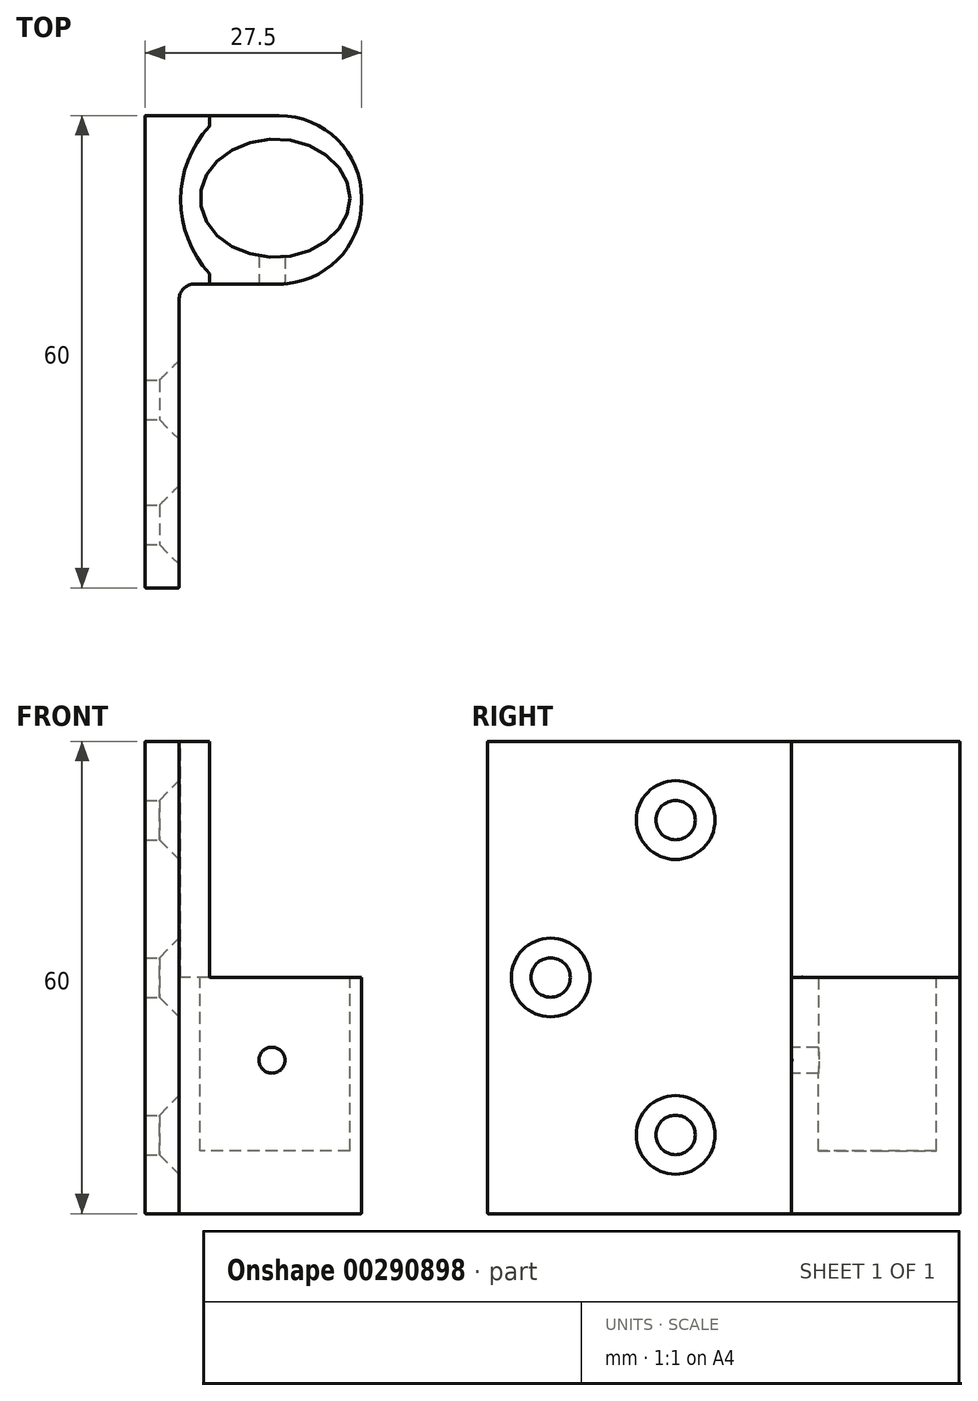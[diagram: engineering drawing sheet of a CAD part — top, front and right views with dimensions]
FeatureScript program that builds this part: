
annotation { "Feature Type Name" : "Feature", "Feature Type Description" : "" }
export const myFeature = defineFeature(function(context is Context, id is Id, definition is map)
    precondition{}
    {
        {
            var Q0;
            Q0=qCreatedBy(makeId("Top.planeOp"),FACE);
            var sketch = newSketch(context, id + "F0", { "sketchPlane" : qUnion([Q0])});
            skLineSegment(sketch, "E0", {"start": v(23.73, 6) * mm, "end": v(23.73, 6.4) * mm});
            skArc(sketch, "E1.filletArc", {"start": v(13.23, -4.5) * mm, "mid": v(20.66, -1.43) * mm, "end": v(23.73, 6) * mm});
            skArc(sketch, "E2.filletArc", {"start": v(23.73, 6.4) * mm, "mid": v(20.66, 13.82) * mm, "end": v(13.23, 16.9) * mm});
            skLineSegment(sketch, "E3.bottom", {"start": v(-3.77, -43.1) * mm, "end": v(0.53, -43.1) * mm});
            skLineSegment(sketch, "E3.left", {"start": v(-3.77, -43.1) * mm, "end": v(-3.77, 16.9) * mm});
            skLineSegment(sketch, "E3.right", {"start": v(0.53, -43.1) * mm, "end": v(0.53, -6.5) * mm});
            skLineSegment(sketch, "E4", {"start": v(-3.77, 16.9) * mm, "end": v(13.23, 16.9) * mm});
            skLineSegment(sketch, "E5", {"start": v(13.23, -4.5) * mm, "end": v(2.53, -4.5) * mm});
            skPoint(sketch, "E6.visualSharp", {"position": v(0.53, -4.5) * mm});
            skArc(sketch, "E6.filletArc", {"start": v(2.53, -4.5) * mm, "mid": v(1.12, -5.1) * mm, "end": v(0.53, -6.5) * mm});
            skSolve(sketch);
        }
        {
            var Q0;
            Q0 = qSketchRegion(id + "F0", true);
            extrude(context, id + "F1", {"entities" : qUnion([Q0]), "depth" : 60 * mm});
        }
        {
            var Q0;
            Q0=makeQuery(id+"F1.opExtrude","CAP_FACE",FACE,{"disambiguationData":[OSD([sQuery(id+"F0.wireOp",EDGE,"E0"),sQuery(id+"F0.wireOp",EDGE,"E1.filletArc"),sQuery(id+"F0.wireOp",EDGE,"E2.filletArc"),sQuery(id+"F0.wireOp",EDGE,"E3.bottom"),sQuery(id+"F0.wireOp",EDGE,"E3.left"),sQuery(id+"F0.wireOp",EDGE,"E3.right"),sQuery(id+"F0.wireOp",EDGE,"E4"),sQuery(id+"F0.wireOp",EDGE,"E5"),sQuery(id+"F0.wireOp",EDGE,"E6.filletArc")])],"isStart":false});
            var sketch = newSketch(context, id + "F2", { "sketchPlane" : qUnion([Q0])});
            skLineSegment(sketch, "E7", {"start": v(4.43, 16.9) * mm, "end": v(4.43, 15.6) * mm});
            skLineSegment(sketch, "E8", {"start": v(-3.77, -4.5) * mm, "end": v(4.43, -4.5) * mm});
            skArc(sketch, "E9", {"start": v(4.43, 15.6) * mm, "mid": v(0.73, 6.2) * mm, "end": v(4.43, -3.2) * mm});
            skLineSegment(sketch, "E10", {"start": v(4.43, 16.9) * mm, "end": v(-3.77, 16.9) * mm});
            skLineSegment(sketch, "E11", {"start": v(-3.77, 16.9) * mm, "end": v(-3.77, -4.5) * mm});
            skLineSegment(sketch, "E12.trimOffspring", {"start": v(4.43, -3.2) * mm, "end": v(4.43, -4.5) * mm});
            skSolve(sketch);
        }
        {
            var Q0;
            {var subQ3=sQuery(id+"F2.wireOp",EDGE,"E7");Q0=makeQuery(id+"F2.imprint","IMPRINT",FACE,{"disambiguationData":[TD([[makeQuery(id+"F2.imprint","IMPRINT",EDGE,{"derivedFrom":subQ3}),1.0]])]});}
            extrude(context, id + "F3", {"entities" : qUnion([Q0]), "operationType" : NewBodyOperationType.REMOVE, "oppositeDirection" : true, "depth" : 30 * mm});
        }
        {
            var Q0;
            Q0=makeQuery(id+"F3.boolean.opBoolean","COPY",FACE,{"derivedFrom":makeQuery(id+"F3.opExtrude","CAP_FACE",FACE,{"disambiguationData":[OSD([sQuery(id+"F0.wireOp",EDGE,"E0"),sQuery(id+"F0.wireOp",EDGE,"E1.filletArc"),sQuery(id+"F0.wireOp",EDGE,"E2.filletArc"),sQuery(id+"F0.wireOp",EDGE,"E4"),sQuery(id+"F0.wireOp",EDGE,"E5"),sQuery(id+"F2.wireOp",EDGE,"E7"),sQuery(id+"F2.wireOp",EDGE,"E9"),sQuery(id+"F2.wireOp",EDGE,"E12.trimOffspring")])],"isStart":false})});
            var sketch = newSketch(context, id + "F4", { "sketchPlane" : qUnion([Q0])});
            skEllipse(sketch, "E13", {"center": v(12.73, 6.4) * mm, "majorRadius": 9.5 * mm, "minorRadius": 7.5 * mm, "majorAxis": v(1, 0)});
            skSolve(sketch);
        }
        {
            var Q0;
            Q0=makeQuery(id+"F4.imprint","IMPRINT",FACE,{"disambiguationData":[TD([[makeQuery(id+"F4.imprint","IMPRINT",EDGE,{"derivedFrom":sQuery(id+"F4.wireOp",EDGE,"E13")}),1.0]])]});
            extrude(context, id + "F5", {"entities" : qUnion([Q0]), "operationType" : NewBodyOperationType.REMOVE, "oppositeDirection" : true, "depth" : 22 * mm});
        }
        {
            var Q0;
            Q0=makeQuery(id+"F1.opExtrude","SWEPT_FACE",FACE,{"disambiguationData":[OSD([sQuery(id+"F0.wireOp",EDGE,"E5")])]});
            var sketch = newSketch(context, id + "F6", { "sketchPlane" : qUnion([Q0])});
            skCircle(sketch, "E14", {"center": v(12.33, 19.5) * mm, "radius": 1.5 * mm});
            skSolve(sketch);
        }
        {
            var Q0;
            Q0=sQuery(id+"F6.wireOp",VERTEX,"E14.center");
            var Q1;
            Q1=makeQuery(id+"F1.opExtrude","SWEPT_BODY",BODY,{"disambiguationData":[OSD([sQuery(id+"F0.wireOp",EDGE,"E0"),sQuery(id+"F0.wireOp",EDGE,"E1.filletArc"),sQuery(id+"F0.wireOp",EDGE,"E2.filletArc"),sQuery(id+"F0.wireOp",EDGE,"E3.bottom"),sQuery(id+"F0.wireOp",EDGE,"E3.left"),sQuery(id+"F0.wireOp",EDGE,"E3.right"),sQuery(id+"F0.wireOp",EDGE,"E4"),sQuery(id+"F0.wireOp",EDGE,"E5"),sQuery(id+"F0.wireOp",EDGE,"E6.filletArc")])]});
            hole(context, id + "F7", {"style" : HoleStyle.SIMPLE, "endStyle" : HoleEndStyle.BLIND, "standardTappedOrClearance" : lookupTablePath({ "standard" : "ISO", "fit" : "Normal", "size" : "M3", "type" : "Clearance" }), "standardBlindInLast" : lookupTablePath({ "fit" : "Standard", "standard" : "ISO", "size" : "M3", "type" : "Clearance" }), "holeDiameter" : 3.3 * mm, "holeDepth" : 8 * mm, "tappedDepth" : 10 * mm, "tapClearance" : 3, "locations" : qUnion([Q0]), "scope" : qUnion([Q1])});
        }
        {
            var Q0;
            Q0=makeQuery(id+"F1.opExtrude","SWEPT_FACE",FACE,{"disambiguationData":[OSD([sQuery(id+"F0.wireOp",EDGE,"E3.right")])]});
            var sketch = newSketch(context, id + "F8", { "sketchPlane" : qUnion([Q0])});
            skCircle(sketch, "E15", {"center": v(-19.23, 50) * mm, "radius": 2.5 * mm});
            skCircle(sketch, "E16", {"center": v(-35.1, 30) * mm, "radius": 2.5 * mm});
            skCircle(sketch, "E17", {"center": v(-19.23, 10) * mm, "radius": 2.5 * mm});
            skSolve(sketch);
        }
        {
            var Q0;
            Q0=sQuery(id+"F8.wireOp",VERTEX,"E15.center");
            var Q1;
            Q1=sQuery(id+"F8.wireOp",VERTEX,"E16.center");
            var Q2;
            Q2=sQuery(id+"F8.wireOp",VERTEX,"E17.center");
            var Q3;
            Q3=makeQuery(id+"F1.opExtrude","SWEPT_BODY",BODY,{"disambiguationData":[OSD([sQuery(id+"F0.wireOp",EDGE,"E0"),sQuery(id+"F0.wireOp",EDGE,"E1.filletArc"),sQuery(id+"F0.wireOp",EDGE,"E2.filletArc"),sQuery(id+"F0.wireOp",EDGE,"E3.bottom"),sQuery(id+"F0.wireOp",EDGE,"E3.left"),sQuery(id+"F0.wireOp",EDGE,"E3.right"),sQuery(id+"F0.wireOp",EDGE,"E4"),sQuery(id+"F0.wireOp",EDGE,"E5"),sQuery(id+"F0.wireOp",EDGE,"E6.filletArc")])]});
            hole(context, id + "F9", {"style" : HoleStyle.C_SINK, "endStyle" : HoleEndStyle.THROUGH, "holeDiameter" : 5 * mm, "cSinkDiameter" : 10 * mm, "cSinkAngle" : 90 * degree, "tappedDepth" : 10 * mm, "tapClearance" : 3, "locations" : qUnion([Q0, Q1, Q2]), "scope" : qUnion([Q3])});
        }
        {
            var Q0;
            Q0=makeQuery(id+"F1.opExtrude","CAP_EDGE",EDGE,{"disambiguationData":[OSD([sQuery(id+"F0.wireOp",EDGE,"E3.right")])],"isStart":false});
            var Q1;
            Q1=makeQuery(id+"F1.opExtrude","SWEPT_EDGE",EDGE,{"disambiguationData":[OSD([sQuery(id+"F0.wireOp",EDGE,"E3.bottom"),sQuery(id+"F0.wireOp",EDGE,"E3.right")])]});
            var Q2;
            Q2=makeQuery(id+"F1.opExtrude","CAP_EDGE",EDGE,{"disambiguationData":[OSD([sQuery(id+"F0.wireOp",EDGE,"E3.bottom")])],"isStart":false});
            var Q3;
            Q3=makeQuery(id+"F1.opExtrude","SWEPT_EDGE",EDGE,{"disambiguationData":[OSD([sQuery(id+"F0.wireOp",EDGE,"E3.bottom"),sQuery(id+"F0.wireOp",EDGE,"E3.left")])]});
            var Q4;
            Q4=makeQuery(id+"F1.opExtrude","CAP_EDGE",EDGE,{"disambiguationData":[OSD([sQuery(id+"F0.wireOp",EDGE,"E3.left")])],"isStart":false});
            var Q5;
            Q5=makeQuery(id+"F1.opExtrude","CAP_EDGE",EDGE,{"disambiguationData":[OSD([sQuery(id+"F0.wireOp",EDGE,"E3.bottom")])],"isStart":true});
            var Q6;
            Q6=makeQuery(id+"F1.opExtrude","CAP_EDGE",EDGE,{"disambiguationData":[OSD([sQuery(id+"F0.wireOp",EDGE,"E3.right")])],"isStart":true});
            var Q7;
            Q7=makeQuery(id+"F1.opExtrude","CAP_EDGE",EDGE,{"disambiguationData":[OSD([sQuery(id+"F0.wireOp",EDGE,"E3.left")])],"isStart":true});
            var Q8;
            Q8=makeQuery(id+"F1.opExtrude","SWEPT_EDGE",EDGE,{"disambiguationData":[OSD([sQuery(id+"F0.wireOp",EDGE,"E3.left"),sQuery(id+"F0.wireOp",EDGE,"E4")])]});
            var Q9;
            Q9=makeQuery(id+"F1.opExtrude","CAP_EDGE",EDGE,{"disambiguationData":[OSD([sQuery(id+"F0.wireOp",EDGE,"E4")])],"isStart":false});
            var Q10;
            Q10=makeQuery(id+"F3.boolean.opBoolean","COPY",EDGE,{"derivedFrom":makeQuery(id+"F3.opExtrude","CAP_EDGE",EDGE,{"disambiguationData":[OSD([sQuery(id+"F2.wireOp",EDGE,"E7")])],"isStart":true})});
            var Q11;
            Q11=makeQuery(id+"F1.opExtrude","CAP_EDGE",EDGE,{"disambiguationData":[OSD([sQuery(id+"F0.wireOp",EDGE,"E4")])],"isStart":true});
            var Q12;
            Q12=makeQuery(id+"F3.boolean.opBoolean","COPY",EDGE,{"derivedFrom":makeQuery(id+"F3.opExtrude","CAP_EDGE",EDGE,{"disambiguationData":[OSD([sQuery(id+"F0.wireOp",EDGE,"E4")])],"isStart":false})});
            var Q13;
            Q13=makeQuery(id+"F5.boolean.opBoolean","COPY",EDGE,{"derivedFrom":makeQuery(id+"F5.opExtrude","CAP_EDGE",EDGE,{"disambiguationData":[OSD([sQuery(id+"F4.wireOp",EDGE,"E13")])],"isStart":true})});
            var Q14;
            Q14=makeQuery(id+"F3.boolean.opBoolean","COPY",EDGE,{"derivedFrom":makeQuery(id+"F3.opExtrude","SWEPT_EDGE",EDGE,{"disambiguationData":[OSD([sQuery(id+"F0.wireOp",EDGE,"E4"),sQuery(id+"F2.wireOp",EDGE,"E7"),sQuery(id+"F2.wireOp",EDGE,"E10")])]})});
            var Q15;
            Q15=makeQuery(id+"F3.boolean.opBoolean","COPY",EDGE,{"derivedFrom":makeQuery(id+"F3.opExtrude","SWEPT_EDGE",EDGE,{"disambiguationData":[OSD([sQuery(id+"F0.wireOp",EDGE,"E5"),sQuery(id+"F2.wireOp",EDGE,"E8"),sQuery(id+"F2.wireOp",EDGE,"E12.trimOffspring")])]})});
            var Q16;
            Q16=makeQuery(id+"F3.boolean.opBoolean","COPY",EDGE,{"derivedFrom":makeQuery(id+"F3.opExtrude","CAP_EDGE",EDGE,{"disambiguationData":[OSD([sQuery(id+"F2.wireOp",EDGE,"E12.trimOffspring")])],"isStart":false})});
            var Q17;
            Q17=makeQuery(id+"F3.boolean.opBoolean","COPY",EDGE,{"derivedFrom":makeQuery(id+"F3.opExtrude","CAP_EDGE",EDGE,{"disambiguationData":[OSD([sQuery(id+"F2.wireOp",EDGE,"E7")])],"isStart":false})});
            var Q18;
            Q18=makeQuery(id+"F3.boolean.opBoolean","COPY",EDGE,{"derivedFrom":makeQuery(id+"F3.opExtrude","CAP_EDGE",EDGE,{"disambiguationData":[OSD([sQuery(id+"F2.wireOp",EDGE,"E12.trimOffspring")])],"isStart":true})});
            var Q19;
            Q19=makeQuery(id+"F3.boolean.opBoolean","COPY",EDGE,{"derivedFrom":makeQuery(id+"F3.opExtrude","CAP_EDGE",EDGE,{"disambiguationData":[OSD([sQuery(id+"F2.wireOp",EDGE,"E9")])],"isStart":true})});
            var Q20;
            Q20=makeQuery(id+"F3.boolean.opBoolean","COPY",EDGE,{"derivedFrom":makeQuery(id+"F3.opExtrude","SWEPT_EDGE",EDGE,{"disambiguationData":[OSD([sQuery(id+"F2.wireOp",EDGE,"E7"),sQuery(id+"F2.wireOp",EDGE,"E9")])]})});
            var Q21;
            Q21=makeQuery(id+"F3.boolean.opBoolean","COPY",EDGE,{"derivedFrom":makeQuery(id+"F3.opExtrude","SWEPT_EDGE",EDGE,{"disambiguationData":[OSD([sQuery(id+"F2.wireOp",EDGE,"E9"),sQuery(id+"F2.wireOp",EDGE,"E12.trimOffspring")])]})});
            fillet(context, id + "F10", {"entities" : qUnion([Q0, Q1, Q2, Q3, Q4, Q5, Q6, Q7, Q8, Q9, Q10, Q11, Q12, Q13, Q14, Q15, Q16, Q17, Q18, Q19, Q20, Q21]), "radius" : 0.1 * mm, "tangentPropagation" : true, "allowEdgeOverflow" : false});
        }
    });
